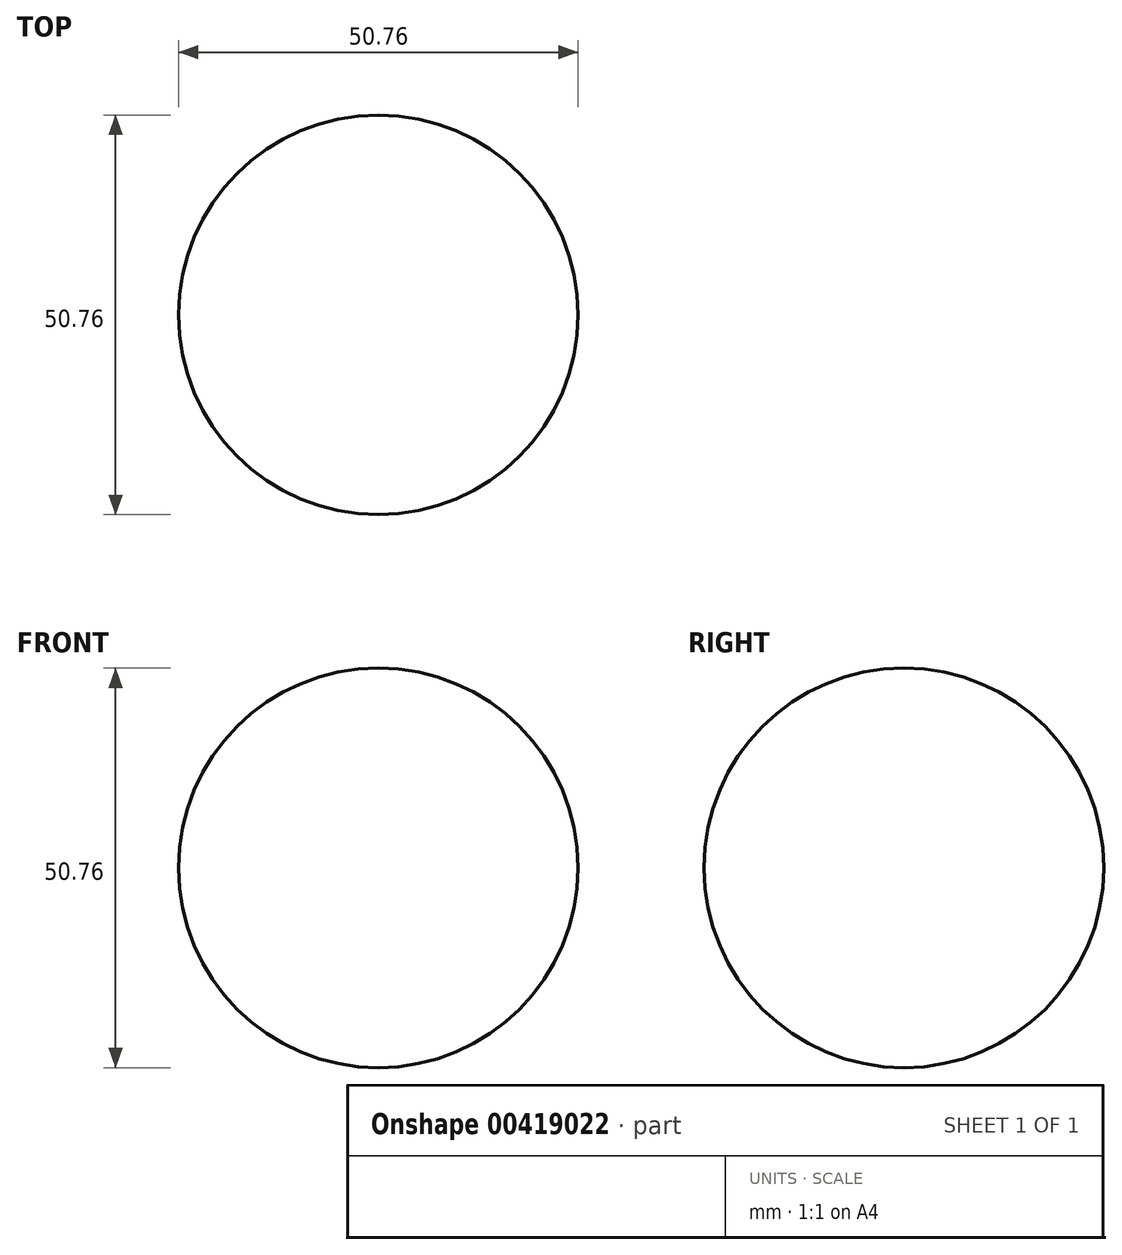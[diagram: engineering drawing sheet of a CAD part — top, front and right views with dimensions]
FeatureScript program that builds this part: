
annotation { "Feature Type Name" : "Feature", "Feature Type Description" : "" }
export const myFeature = defineFeature(function(context is Context, id is Id, definition is map)
    precondition{}
    {
        {
            var Q0;
            Q0=qCreatedBy(makeId("Top.planeOp"),FACE);
            var sketch = newSketch(context, id + "F0", { "sketchPlane" : qUnion([Q0])});
            skArc(sketch, "E0", {"start": v(0, -25.38) * mm, "mid": v(25.38, 0) * mm, "end": v(0, 25.38) * mm});
            skLineSegment(sketch, "E1", {"start": v(0, 28.45) * mm, "end": v(0, -29.98) * mm});
            skSolve(sketch);
        }
        {
            var Q0;
            Q0 = qSketchRegion(id + "F0", true);
            var Q1;
            Q1=sQuery(id+"F0.wireOp",EDGE,"E1");
            revolve(context, id + "F1", {"entities" : qUnion([Q0]), "axis" : qUnion([Q1]), "revolveType" : RevolveType.FULL});
        }
    });
